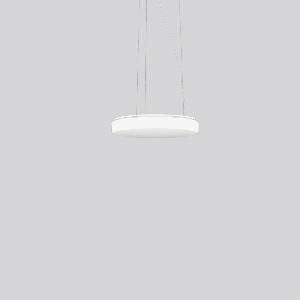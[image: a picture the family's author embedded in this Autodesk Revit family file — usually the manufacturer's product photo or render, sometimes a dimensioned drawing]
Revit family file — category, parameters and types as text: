
# Revit family: flat_polymero_kreis_slim_312089_002_1_88c0
name_source: partatom
category: Lighting Fixtures
units: mm (PartAtom-declared; Revit-internal decimal feet)

## family parameters
Cut with Voids When Loaded = No
Host = Face
Light Source = No
Part Type = Normal
Room Calculation Point = No
Round Connector Dimension = Use Diameter
Shared = No

## types (1)
- FLAT POLYMERO KREIS SLIM (1 x LED Modul 830, 1900 lm, 3000)
    Apparent Load = 19 VA
    CIE Flux Codes = 42 73 92 85 100
    Color Rendering = 80
    Color Temperature = 3000
    Default Elevation = 1800 mm
    Description = Series: FLAT POLYMERO KREIS SLIM
Decorative round LED pendant luminaire. Base and canopy: metal, powder-coated, white. Canopy Ø 205 mm, h 35 mm. Diffuser made of non-yellowing plastic (PMMA), opal. Diffuser fastening: patented push system. Homogeneous and smooth light distribution. Suitable for pendant. 3-point steel cable suspension, steplessly adjustable. Special lengths available on request. 
Colour: white
Diameter: 360 mm
Height: 61 mm
Suspension length: 200-1300 mm
Lamp: LED
Socket: without socket
Colour temperature: 3000K
Colour rendering index (CRI): 80
System power: 19 W
Rated luminous flux: 1900 lm
Luminous efficiency: 100 lm/W
Control gear: AC Strom, dim.Ph.an-/abschnitt
Protection class: I
Type of protection: IP 40
    Height = 61 mm
    Lamp = 1 x LED Modul 830
    Lamp Light Flux = 1900 lm
    Lamp count = 1
    Length = 360 mm
    Lifetime = 50000 h
    Luminous efficacy = 100 lm/W
    Manufacturer = RZB
    ModVariant = No
    Model = 312089.002.1
    Mounting Place = Ceiling
    Mounting Type = Pendant
    Number of Poles = 1
    OnlyDefault = Yes
    Power Factor = 1
    Product Name = FLAT POLYMERO KREIS SLIM
    Product group = Pendant luminaires
    ProductGroupID = 902
    Protection Class = Protection class I
    Protection Degree = IP 40
    RLX_Detail_Level = 1
    RLX_Emergency_Light_Flux = 0 lm
    RLX_Emergency_Type = 0
    RLX_Emergency_Type_DB = No
    RlxData = <blob elided: 56049 chars, md5=1f39780a>
    Socket = socket
    Standby Power = 0 W
    System Light Flux = 1900 lm
    System Power = 19 W
    Type Comments = Product without accessories
    Type Image = 312089.002.jpg
    URL = http://relux.com
    VarID = ---
    Voltage = 230 V
    Voltage Range = 220-240 V
    Weight = 0.00 kg
    Width = 0 mm  [stored 0 ft]

note: [stored X ft] marks values corroborated as IEEE doubles in the binary element streams (Revit-internal decimal feet)

## geometry (parser evidence)
native form markers: Blend x4, Sweep x12
no freeform markers — native parametric forms only
